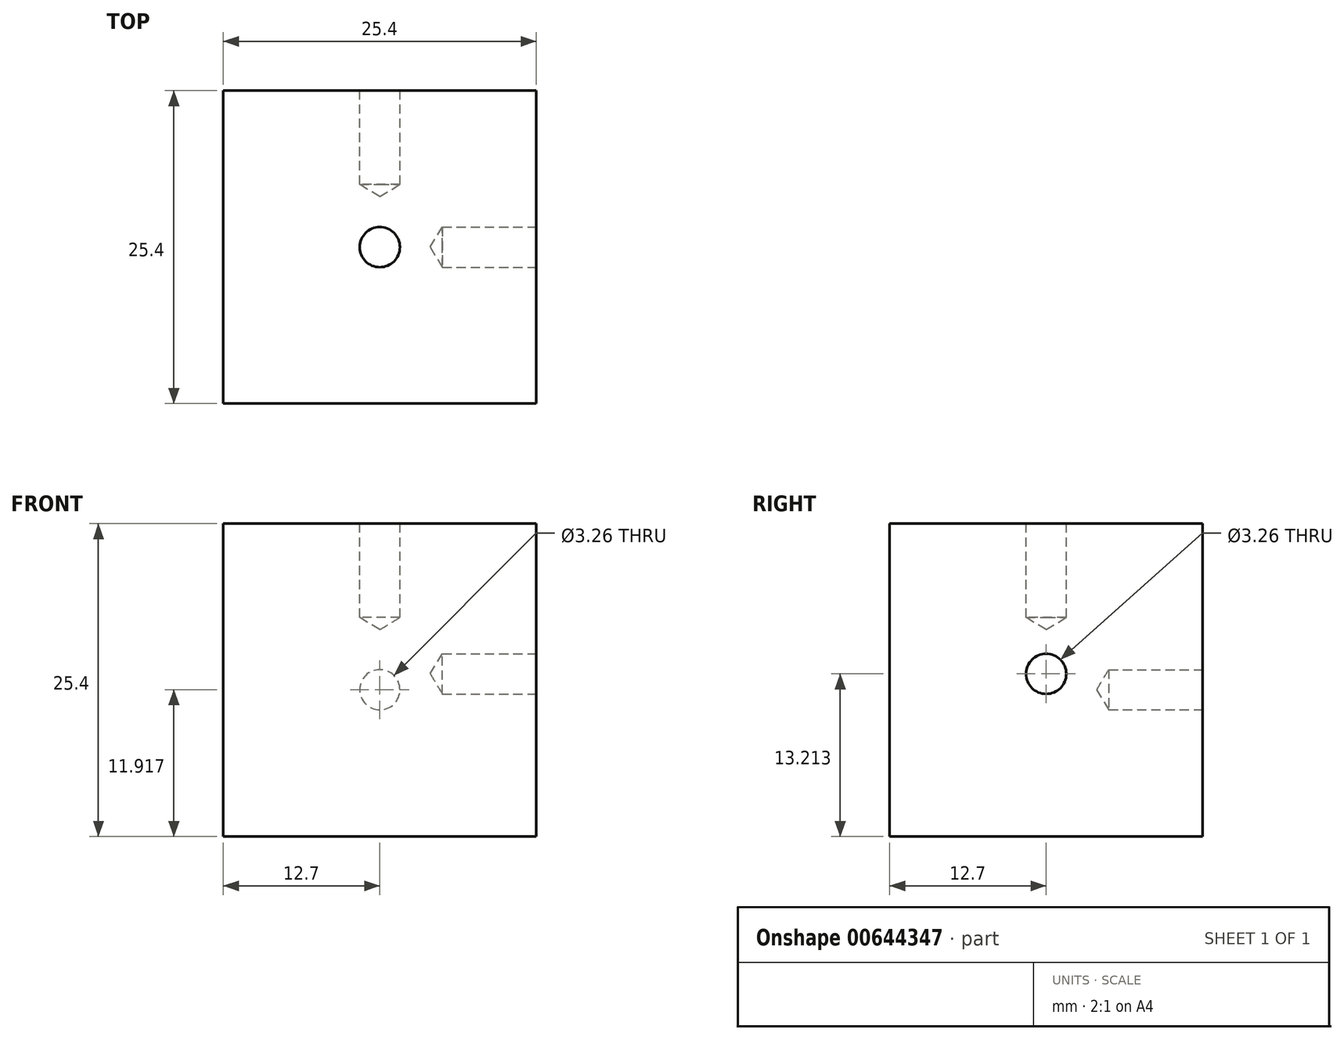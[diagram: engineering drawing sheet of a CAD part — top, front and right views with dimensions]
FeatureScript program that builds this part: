
annotation { "Feature Type Name" : "Feature", "Feature Type Description" : "" }
export const myFeature = defineFeature(function(context is Context, id is Id, definition is map)
    precondition{}
    {
        {
            var Q0;
            Q0=qCreatedBy(makeId("Top.planeOp"),FACE);
            var sketch = newSketch(context, id + "F0", { "sketchPlane" : qUnion([Q0])});
            skLineSegment(sketch, "E0.bottom", {"start": v(-12.7, 12.7) * mm, "end": v(12.7, 12.7) * mm});
            skLineSegment(sketch, "E0.top", {"start": v(-12.7, -12.7) * mm, "end": v(12.7, -12.7) * mm});
            skLineSegment(sketch, "E0.left", {"start": v(-12.7, 12.7) * mm, "end": v(-12.7, -12.7) * mm});
            skLineSegment(sketch, "E0.right", {"start": v(12.7, 12.7) * mm, "end": v(12.7, -12.7) * mm});
            skPoint(sketch, "E0.middle", {"position": v(0, 0) * mm});
            skSolve(sketch);
        }
        {
            var Q0;
            Q0 = qSketchRegion(id + "F0", true);
            extrude(context, id + "F1", {"entities" : qUnion([Q0]), "depth" : 25.4 * mm, "offsetDistance" : 25.4 * mm});
        }
        {
            var Q0;
            Q0=makeQuery(id+"F1.opExtrude","CAP_FACE",FACE,{"disambiguationData":[OSD([sQuery(id+"F0.wireOp",EDGE,"E0.bottom"),sQuery(id+"F0.wireOp",EDGE,"E0.top"),sQuery(id+"F0.wireOp",EDGE,"E0.left"),sQuery(id+"F0.wireOp",EDGE,"E0.right")])],"isStart":false});
            var sketch = newSketch(context, id + "F2", { "sketchPlane" : qUnion([Q0])});
            skPoint(sketch, "E1", {"position": v(0, 0) * mm});
            skSolve(sketch);
        }
        {
            var Q0;
            Q0=makeQuery(id+"F1.opExtrude","SWEPT_FACE",FACE,{"disambiguationData":[OSD([sQuery(id+"F0.wireOp",EDGE,"E0.right")])]});
            var sketch = newSketch(context, id + "F3", { "sketchPlane" : qUnion([Q0])});
            skPoint(sketch, "E2", {"position": v(0, 13.21) * mm});
            skSolve(sketch);
        }
        {
            var Q0;
            Q0=makeQuery(id+"F1.opExtrude","SWEPT_FACE",FACE,{"disambiguationData":[OSD([sQuery(id+"F0.wireOp",EDGE,"E0.bottom")])]});
            var sketch = newSketch(context, id + "F4", { "sketchPlane" : qUnion([Q0])});
            skPoint(sketch, "E3", {"position": v(0, 11.92) * mm});
            skSolve(sketch);
        }
        {
            var Q0;
            Q0=sQuery(id+"F2.wireOp",VERTEX,"E1");
            var Q1;
            Q1=makeQuery(id+"F1.opExtrude","SWEPT_BODY",BODY,{"disambiguationData":[OSD([sQuery(id+"F0.wireOp",EDGE,"E0.bottom"),sQuery(id+"F0.wireOp",EDGE,"E0.top"),sQuery(id+"F0.wireOp",EDGE,"E0.left"),sQuery(id+"F0.wireOp",EDGE,"E0.right")])]});
            hole(context, id + "F5", {"style" : HoleStyle.SIMPLE, "endStyle" : HoleEndStyle.BLIND, "standardTappedOrClearance" : lookupTablePath({ "standard" : "ANSI", "fit" : "Normal (ASME)", "size" : "#4", "type" : "Clearance" }), "standardBlindInLast" : lookupTablePath({ "fit" : "Free", "standard" : "ANSI", "size" : "#4", "type" : "Clearance" }), "holeDiameter" : 3.26 * mm, "majorDiameter" : 6.35 * mm, "holeDepth" : 7.62 * mm, "tappedDepth" : 10.3 * mm, "tapClearance" : 3, "locations" : qUnion([Q0]), "scope" : qUnion([Q1])});
        }
        {
            var Q0;
            Q0=sQuery(id+"F3.wireOp",VERTEX,"E2");
            var Q1;
            Q1=makeQuery(id+"F1.opExtrude","SWEPT_BODY",BODY,{"disambiguationData":[OSD([sQuery(id+"F0.wireOp",EDGE,"E0.bottom"),sQuery(id+"F0.wireOp",EDGE,"E0.top"),sQuery(id+"F0.wireOp",EDGE,"E0.left"),sQuery(id+"F0.wireOp",EDGE,"E0.right")])]});
            hole(context, id + "F6", {"style" : HoleStyle.SIMPLE, "endStyle" : HoleEndStyle.BLIND, "standardTappedOrClearance" : lookupTablePath({ "standard" : "ANSI", "fit" : "Normal (ASME)", "size" : "#4", "type" : "Clearance" }), "standardBlindInLast" : lookupTablePath({ "fit" : "Free", "standard" : "ANSI", "size" : "#4", "type" : "Clearance" }), "holeDiameter" : 3.26 * mm, "majorDiameter" : 6.35 * mm, "holeDepth" : 7.62 * mm, "tappedDepth" : 10.3 * mm, "tapClearance" : 3, "locations" : qUnion([Q0]), "scope" : qUnion([Q1])});
        }
        {
            var Q0;
            Q0=sQuery(id+"F4.wireOp",VERTEX,"E3");
            var Q1;
            Q1=makeQuery(id+"F1.opExtrude","SWEPT_BODY",BODY,{"disambiguationData":[OSD([sQuery(id+"F0.wireOp",EDGE,"E0.bottom"),sQuery(id+"F0.wireOp",EDGE,"E0.top"),sQuery(id+"F0.wireOp",EDGE,"E0.left"),sQuery(id+"F0.wireOp",EDGE,"E0.right")])]});
            hole(context, id + "F7", {"style" : HoleStyle.SIMPLE, "endStyle" : HoleEndStyle.BLIND, "standardTappedOrClearance" : lookupTablePath({ "standard" : "ANSI", "fit" : "Normal (ASME)", "size" : "#4", "type" : "Clearance" }), "standardBlindInLast" : lookupTablePath({ "fit" : "Free", "standard" : "ANSI", "size" : "#4", "type" : "Clearance" }), "holeDiameter" : 3.26 * mm, "majorDiameter" : 6.35 * mm, "holeDepth" : 7.62 * mm, "tappedDepth" : 10.3 * mm, "tapClearance" : 3, "locations" : qUnion([Q0]), "scope" : qUnion([Q1])});
        }
    });
